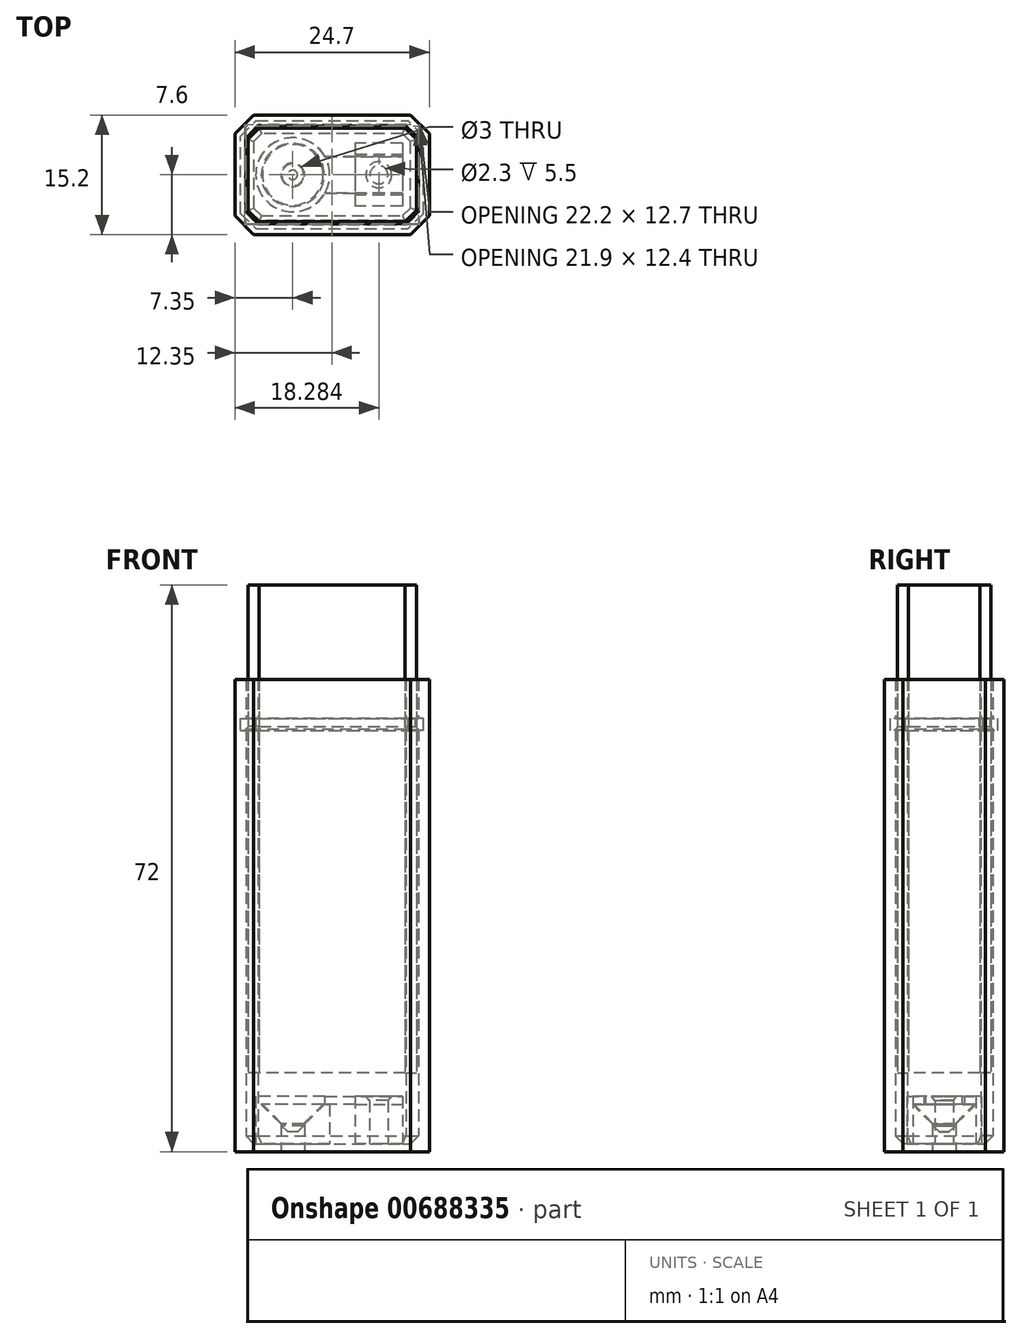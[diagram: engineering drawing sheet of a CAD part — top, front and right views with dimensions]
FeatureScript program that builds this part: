
annotation { "Feature Type Name" : "Feature", "Feature Type Description" : "" }
export const myFeature = defineFeature(function(context is Context, id is Id, definition is map)
    precondition{}
    {
        {
            var Q0;
            Q0=qCreatedBy(makeId("Top.planeOp"),FACE);
            cPlane(context, id + "F0", {"entities" : qUnion([Q0]), "cplaneType" : CPlaneType.OFFSET, "offset" : 10 * mm, "width" : 150 * mm, "height" : 150 * mm});
        }
        {
            var Q0;
            Q0=qCreatedBy(id+"F0.planeOp",FACE);
            var sketch = newSketch(context, id + "F1", { "sketchPlane" : qUnion([Q0])});
            skLineSegment(sketch, "E0.bottom", {"start": v(9.29, 5.95) * mm, "end": v(-9.29, 5.95) * mm});
            skLineSegment(sketch, "E0.top", {"start": v(9.29, -5.95) * mm, "end": v(-9.29, -5.95) * mm});
            skLineSegment(sketch, "E0.left", {"start": v(10.7, 4.54) * mm, "end": v(10.7, -4.54) * mm});
            skLineSegment(sketch, "E0.right", {"start": v(-10.7, 4.54) * mm, "end": v(-10.7, -4.54) * mm});
            skPoint(sketch, "E0.middle", {"position": v(0, 0) * mm});
            skLineSegment(sketch, "E1", {"start": v(9.29, 5.95) * mm, "end": v(10.7, 4.54) * mm});
            skPoint(sketch, "E2.orphan", {"position": v(10.7, 5.95) * mm});
            skLineSegment(sketch, "E3.MirrorCS", {"start": v(9.29, -5.95) * mm, "end": v(10.7, -4.54) * mm});
            skLineSegment(sketch, "E4.MirrorCS", {"start": v(-9.29, 5.95) * mm, "end": v(-10.7, 4.54) * mm});
            skLineSegment(sketch, "E5.MirrorCS", {"start": v(-9.29, -5.95) * mm, "end": v(-10.7, -4.54) * mm});
            skPoint(sketch, "E6.orphan", {"position": v(10.7, -5.95) * mm});
            skPoint(sketch, "E7.orphan", {"position": v(-10.7, -5.95) * mm});
            skPoint(sketch, "E8.orphan", {"position": v(-10.7, 5.95) * mm});
            skSolve(sketch);
        }
        {
            var Q0;
            Q0=makeQuery(id+"F1.imprint","IMPRINT",FACE,{"disambiguationData":[TD([[makeQuery(id+"F1.imprint","IMPRINT",EDGE,{"derivedFrom":sQuery(id+"F1.wireOp",EDGE,"E0.bottom")}),1.0]])]});
            extrude(context, id + "F2", {"entities" : qUnion([Q0]), "depth" : 62 * mm, "offsetDistance" : 25 * mm});
        }
        {
            var Q0;
            Q0=qCreatedBy(makeId("Top.planeOp"),FACE);
            var sketch = newSketch(context, id + "F3", { "sketchPlane" : qUnion([Q0])});
            skLineSegment(sketch, "E9.0", {"start": v(12.35, -5.22) * mm, "end": v(9.97, -7.6) * mm});
            skLineSegment(sketch, "E9.1", {"start": v(12.35, 5.22) * mm, "end": v(12.35, -5.22) * mm});
            skLineSegment(sketch, "E9.2", {"start": v(9.97, -7.6) * mm, "end": v(-9.97, -7.6) * mm});
            skLineSegment(sketch, "E9.3", {"start": v(9.97, 7.6) * mm, "end": v(12.35, 5.22) * mm});
            skLineSegment(sketch, "E9.4", {"start": v(-9.97, -7.6) * mm, "end": v(-12.35, -5.22) * mm});
            skLineSegment(sketch, "E9.5", {"start": v(-12.35, -5.22) * mm, "end": v(-12.35, 5.22) * mm});
            skLineSegment(sketch, "E9.6", {"start": v(-12.35, 5.22) * mm, "end": v(-9.97, 7.6) * mm});
            skLineSegment(sketch, "E9.7", {"start": v(-9.97, 7.6) * mm, "end": v(9.97, 7.6) * mm});
            skSolve(sketch);
        }
        {
            var Q0;
            Q0=makeQuery(id+"F3.imprint","IMPRINT",FACE,{"disambiguationData":[TD([[makeQuery(id+"F3.imprint","IMPRINT",EDGE,{"derivedFrom":sQuery(id+"F3.wireOp",EDGE,"E9.0")}),-1.0]])]});
            extrude(context, id + "F4", {"entities" : qUnion([Q0]), "depth" : 60 * mm, "offsetDistance" : 25 * mm});
        }
        {
            var Q0;
            Q0=makeQuery(id+"F2.opExtrude","SWEPT_BODY",BODY,{"disambiguationData":[OSD([sQuery(id+"F1.wireOp",EDGE,"E0.bottom"),sQuery(id+"F1.wireOp",EDGE,"E0.top"),sQuery(id+"F1.wireOp",EDGE,"E0.left"),sQuery(id+"F1.wireOp",EDGE,"E0.right"),sQuery(id+"F1.wireOp",EDGE,"E1"),sQuery(id+"F1.wireOp",EDGE,"E3.MirrorCS"),sQuery(id+"F1.wireOp",EDGE,"E4.MirrorCS"),sQuery(id+"F1.wireOp",EDGE,"E5.MirrorCS")])]});
            var Q1;
            Q1=makeQuery(id+"F4.opExtrude","SWEPT_BODY",BODY,{"disambiguationData":[OSD([sQuery(id+"F3.wireOp",EDGE,"E9.0"),sQuery(id+"F3.wireOp",EDGE,"E9.1"),sQuery(id+"F3.wireOp",EDGE,"E9.2"),sQuery(id+"F3.wireOp",EDGE,"E9.3"),sQuery(id+"F3.wireOp",EDGE,"E9.4"),sQuery(id+"F3.wireOp",EDGE,"E9.5"),sQuery(id+"F3.wireOp",EDGE,"E9.6"),sQuery(id+"F3.wireOp",EDGE,"E9.7")])]});
            var Q2;
            Q2=makeQuery(id+"F2.opExtrude","SWEPT_FACE",FACE,{"disambiguationData":[OSD([sQuery(id+"F1.wireOp",EDGE,"E0.top")])]});
            var Q3;
            Q3=makeQuery(id+"F2.opExtrude","SWEPT_FACE",FACE,{"disambiguationData":[OSD([sQuery(id+"F1.wireOp",EDGE,"E3.MirrorCS")])]});
            var Q4;
            Q4=makeQuery(id+"F2.opExtrude","SWEPT_FACE",FACE,{"disambiguationData":[OSD([sQuery(id+"F1.wireOp",EDGE,"E0.left")])]});
            var Q5;
            Q5=makeQuery(id+"F2.opExtrude","SWEPT_FACE",FACE,{"disambiguationData":[OSD([sQuery(id+"F1.wireOp",EDGE,"E0.bottom")])]});
            var Q6;
            Q6=makeQuery(id+"F2.opExtrude","SWEPT_FACE",FACE,{"disambiguationData":[OSD([sQuery(id+"F1.wireOp",EDGE,"E4.MirrorCS")])]});
            var Q7;
            Q7=makeQuery(id+"F2.opExtrude","SWEPT_FACE",FACE,{"disambiguationData":[OSD([sQuery(id+"F1.wireOp",EDGE,"E0.right")])]});
            var Q8;
            Q8=makeQuery(id+"F2.opExtrude","SWEPT_FACE",FACE,{"disambiguationData":[OSD([sQuery(id+"F1.wireOp",EDGE,"E5.MirrorCS")])]});
            var Q9;
            Q9=makeQuery(id+"F2.opExtrude","SWEPT_FACE",FACE,{"disambiguationData":[OSD([sQuery(id+"F1.wireOp",EDGE,"E1")])]});
            booleanBodies(context, id + "F5", {"operationType" : BooleanOperationType.SUBTRACTION, "tools" : qUnion([Q0]), "targets" : qUnion([Q1]), "offset" : true, "entitiesToOffset" : qUnion([Q2, Q3, Q4, Q5, Q6, Q7, Q8, Q9]), "offsetDistance" : .25 * mm, "keepTools" : true});
        }
        {
            var Q0;
            Q0=makeQuery(id+"F5.tempBoolean.opBoolean","COPY",FACE,{"derivedFrom":makeQuery(id+"F5.offsetTempBody.opPattern","COPY",FACE,{"derivedFrom":makeQuery(id+"F2.opExtrude","CAP_FACE",FACE,{"disambiguationData":[OSD([sQuery(id+"F1.wireOp",EDGE,"E0.bottom"),sQuery(id+"F1.wireOp",EDGE,"E0.top"),sQuery(id+"F1.wireOp",EDGE,"E0.left"),sQuery(id+"F1.wireOp",EDGE,"E0.right"),sQuery(id+"F1.wireOp",EDGE,"E1"),sQuery(id+"F1.wireOp",EDGE,"E3.MirrorCS"),sQuery(id+"F1.wireOp",EDGE,"E4.MirrorCS"),sQuery(id+"F1.wireOp",EDGE,"E5.MirrorCS")])],"isStart":true}),"instanceName":"1"})});
            var Q1;
            Q1=makeQuery(id+"F4.opExtrude","CAP_FACE",FACE,{"disambiguationData":[OSD([sQuery(id+"F3.wireOp",EDGE,"E9.0"),sQuery(id+"F3.wireOp",EDGE,"E9.1"),sQuery(id+"F3.wireOp",EDGE,"E9.2"),sQuery(id+"F3.wireOp",EDGE,"E9.3"),sQuery(id+"F3.wireOp",EDGE,"E9.4"),sQuery(id+"F3.wireOp",EDGE,"E9.5"),sQuery(id+"F3.wireOp",EDGE,"E9.6"),sQuery(id+"F3.wireOp",EDGE,"E9.7")])],"isStart":true});
            extrude(context, id + "F6", {"entities" : qUnion([Q0]), "operationType" : NewBodyOperationType.REMOVE, "endBound" : BoundingType.UP_TO_SURFACE, "oppositeDirection" : true, "depth" : 25 * mm, "endBoundEntityFace" : qUnion([Q1]), "hasOffset" : true, "offsetDistance" : 1 * mm});
        }
        {
            var Q0;
            Q0=makeQuery(id+"F6.boolean.opBoolean","COPY",EDGE,{"derivedFrom":makeQuery(id+"F6.opExtrude","CAP_EDGE",EDGE,{"disambiguationData":[OSD([sQuery(id+"F1.wireOp",EDGE,"E0.left")])],"isStart":false})});
            var Q1;
            Q1=makeQuery(id+"F6.boolean.opBoolean","COPY",EDGE,{"derivedFrom":makeQuery(id+"F6.opExtrude","CAP_EDGE",EDGE,{"disambiguationData":[OSD([sQuery(id+"F1.wireOp",EDGE,"E3.MirrorCS")])],"isStart":false})});
            var Q2;
            Q2=makeQuery(id+"F6.boolean.opBoolean","COPY",EDGE,{"derivedFrom":makeQuery(id+"F6.opExtrude","CAP_EDGE",EDGE,{"disambiguationData":[OSD([sQuery(id+"F1.wireOp",EDGE,"E0.top")])],"isStart":false})});
            var Q3;
            Q3=makeQuery(id+"F6.boolean.opBoolean","COPY",EDGE,{"derivedFrom":makeQuery(id+"F6.opExtrude","CAP_EDGE",EDGE,{"disambiguationData":[OSD([sQuery(id+"F1.wireOp",EDGE,"E5.MirrorCS")])],"isStart":false})});
            var Q4;
            Q4=makeQuery(id+"F6.boolean.opBoolean","COPY",EDGE,{"derivedFrom":makeQuery(id+"F6.opExtrude","CAP_EDGE",EDGE,{"disambiguationData":[OSD([sQuery(id+"F1.wireOp",EDGE,"E0.right")])],"isStart":false})});
            var Q5;
            Q5=makeQuery(id+"F6.boolean.opBoolean","COPY",EDGE,{"derivedFrom":makeQuery(id+"F6.opExtrude","CAP_EDGE",EDGE,{"disambiguationData":[OSD([sQuery(id+"F1.wireOp",EDGE,"E4.MirrorCS")])],"isStart":false})});
            var Q6;
            Q6=makeQuery(id+"F6.boolean.opBoolean","COPY",EDGE,{"derivedFrom":makeQuery(id+"F6.opExtrude","CAP_EDGE",EDGE,{"disambiguationData":[OSD([sQuery(id+"F1.wireOp",EDGE,"E0.bottom")])],"isStart":false})});
            var Q7;
            Q7=makeQuery(id+"F6.boolean.opBoolean","COPY",EDGE,{"derivedFrom":makeQuery(id+"F6.opExtrude","CAP_EDGE",EDGE,{"disambiguationData":[OSD([sQuery(id+"F1.wireOp",EDGE,"E1")])],"isStart":false})});
            chamfer(context, id + "F7", {"entities" : qUnion([Q0, Q1, Q2, Q3, Q4, Q5, Q6, Q7]), "width" : 1 * mm, "tangentPropagation" : true});
        }
        {
            var Q0;
            Q0=makeQuery(id+"F6.boolean.opBoolean","COPY",FACE,{"derivedFrom":makeQuery(id+"F6.opExtrude","CAP_FACE",FACE,{"disambiguationData":[OSD([sQuery(id+"F1.wireOp",EDGE,"E0.bottom"),sQuery(id+"F1.wireOp",EDGE,"E0.top"),sQuery(id+"F1.wireOp",EDGE,"E0.left"),sQuery(id+"F1.wireOp",EDGE,"E0.right"),sQuery(id+"F1.wireOp",EDGE,"E1"),sQuery(id+"F1.wireOp",EDGE,"E3.MirrorCS"),sQuery(id+"F1.wireOp",EDGE,"E4.MirrorCS"),sQuery(id+"F1.wireOp",EDGE,"E5.MirrorCS")])],"isStart":false})});
            var sketch = newSketch(context, id + "F8", { "sketchPlane" : qUnion([Q0])});
            skCircle(sketch, "E10", {"center": v(-5, 0) * mm, "radius": 1.5 * mm});
            skCircle(sketch, "E11", {"center": v(-5, 0) * mm, "radius": 4.7 * mm});
            skSolve(sketch);
        }
        {
            var Q0;
            Q0=makeQuery(id+"F8.imprint","IMPRINT",FACE,{"disambiguationData":[TD([[makeQuery(id+"F8.imprint","IMPRINT",EDGE,{"derivedFrom":sQuery(id+"F8.wireOp",EDGE,"E10")}),-1.0]])]});
            extrude(context, id + "F9", {"entities" : qUnion([Q0]), "operationType" : NewBodyOperationType.ADD, "depth" : 5 * mm, "offsetDistance" : 25 * mm});
        }
        {
            var Q0;
            Q0=makeQuery(id+"F9.boolean.opBoolean","SPLIT",FACE,{"disambiguationData":[TD([makeQuery(id+"F9.opExtrude","SWEPT_FACE",FACE,{"disambiguationData":[OSD([sQuery(id+"F8.wireOp",EDGE,"E10")])]})])],"derivedFrom":makeQuery(id+"F6.boolean.opBoolean","COPY",FACE,{"derivedFrom":makeQuery(id+"F6.opExtrude","CAP_FACE",FACE,{"disambiguationData":[OSD([sQuery(id+"F1.wireOp",EDGE,"E0.bottom"),sQuery(id+"F1.wireOp",EDGE,"E0.top"),sQuery(id+"F1.wireOp",EDGE,"E0.left"),sQuery(id+"F1.wireOp",EDGE,"E0.right"),sQuery(id+"F1.wireOp",EDGE,"E1"),sQuery(id+"F1.wireOp",EDGE,"E3.MirrorCS"),sQuery(id+"F1.wireOp",EDGE,"E4.MirrorCS"),sQuery(id+"F1.wireOp",EDGE,"E5.MirrorCS")])],"isStart":false})})});
            extrude(context, id + "F10", {"entities" : qUnion([Q0]), "operationType" : NewBodyOperationType.REMOVE, "endBound" : BoundingType.THROUGH_ALL, "oppositeDirection" : true, "depth" : 25 * mm, "offsetDistance" : 25 * mm});
        }
        {
            var Q0;
            Q0=makeQuery(id+"F9.opExtrude","CAP_EDGE",EDGE,{"disambiguationData":[OSD([sQuery(id+"F8.wireOp",EDGE,"E10")])],"isStart":false});
            chamfer(context, id + "F11", {"entities" : qUnion([Q0]), "width" : 2.5 * mm, "tangentPropagation" : true});
        }
        {
            var Q0;
            Q0=makeQuery(id+"F9.opExtrude","CAP_FACE",FACE,{"disambiguationData":[OSD([sQuery(id+"F8.wireOp",EDGE,"E10"),sQuery(id+"F8.wireOp",EDGE,"E11")])],"isStart":false});
            var sketch = newSketch(context, id + "F12", { "sketchPlane" : qUnion([Q0])});
            skCircle(sketch, "E12.0", {"center": v(-5, 0) * mm, "radius": 4.7 * mm});
            skSolve(sketch);
        }
        {
            var Q0;
            Q0 = qSketchRegion(id + "F12", true);
            var Q1;
            Q1=makeQuery(id+"F4.opExtrude","CAP_FACE",FACE,{"disambiguationData":[OSD([sQuery(id+"F3.wireOp",EDGE,"E9.0"),sQuery(id+"F3.wireOp",EDGE,"E9.1"),sQuery(id+"F3.wireOp",EDGE,"E9.2"),sQuery(id+"F3.wireOp",EDGE,"E9.3"),sQuery(id+"F3.wireOp",EDGE,"E9.4"),sQuery(id+"F3.wireOp",EDGE,"E9.5"),sQuery(id+"F3.wireOp",EDGE,"E9.6"),sQuery(id+"F3.wireOp",EDGE,"E9.7")])],"isStart":true});
            extrude(context, id + "F13", {"entities" : qUnion([Q0]), "depth" : 1 * mm, "offsetDistance" : 25 * mm, "hasSecondDirection" : true, "secondDirectionBound" : SecondDirectionBoundingType.UP_TO_SURFACE, "secondDirectionOppositeDirection" : true, "secondDirectionDepth" : 25 * mm, "secondDirectionBoundEntityFace" : qUnion([Q1]), "hasSecondDirectionOffset" : true, "secondDirectionOffsetDistance" : 2.5 * mm});
        }
        {
            var Q0;
            Q0=makeQuery(id+"F4.opExtrude","SWEPT_BODY",BODY,{"disambiguationData":[OSD([sQuery(id+"F3.wireOp",EDGE,"E9.0"),sQuery(id+"F3.wireOp",EDGE,"E9.1"),sQuery(id+"F3.wireOp",EDGE,"E9.2"),sQuery(id+"F3.wireOp",EDGE,"E9.3"),sQuery(id+"F3.wireOp",EDGE,"E9.4"),sQuery(id+"F3.wireOp",EDGE,"E9.5"),sQuery(id+"F3.wireOp",EDGE,"E9.6"),sQuery(id+"F3.wireOp",EDGE,"E9.7")])]});
            var Q1;
            Q1=makeQuery(id+"F13.opExtrude","SWEPT_BODY",BODY,{"disambiguationData":[OSD([sQuery(id+"F12.wireOp",EDGE,"E12.0")])]});
            var Q2;
            Q2=makeQuery(id+"F11.opChamfer","BLEND_FACE",FACE,{"disambiguationData":[OSD([sQuery(id+"F8.wireOp",EDGE,"E10")])]});
            var Q3;
            {var subQ0=sQuery(id+"F8.wireOp",EDGE,"E10");Q3=makeQuery(id+"F10.boolean.opBoolean","MERGE",FACE,{"derivedFrom":[makeQuery(id+"F9.opExtrude","SWEPT_FACE",FACE,{"disambiguationData":[OSD([subQ0])]}),makeQuery(id+"F10.opExtrude","SWEPT_FACE",FACE,{"disambiguationData":[OSD([subQ0])]})]});}
            booleanBodies(context, id + "F14", {"operationType" : BooleanOperationType.SUBTRACTION, "tools" : qUnion([Q0]), "targets" : qUnion([Q1]), "offset" : true, "entitiesToOffset" : qUnion([Q2, Q3]), "offsetDistance" : .1 * mm, "keepTools" : true});
        }
        {
            var Q0;
            {var subQ0=sQuery(id+"F8.wireOp",EDGE,"E10");Q0=makeQuery(id+"F14.tempBoolean.opBoolean","INTERSECT",EDGE,{"derivedFrom":[makeQuery(id+"F13.opExtrude","CAP_FACE",FACE,{"disambiguationData":[OSD([sQuery(id+"F12.wireOp",EDGE,"E12.0")])],"isStart":true}),makeQuery(id+"F14.offsetTempBody.opPattern","COPY",FACE,{"derivedFrom":makeQuery(id+"F10.boolean.opBoolean","MERGE",FACE,{"derivedFrom":[makeQuery(id+"F9.opExtrude","SWEPT_FACE",FACE,{"disambiguationData":[OSD([subQ0])]})],"fromTools":[makeQuery(id+"F10.opExtrude","SWEPT_FACE",FACE,{"disambiguationData":[OSD([subQ0])]})]}),"instanceName":"1"})]});}
            chamfer(context, id + "F15", {"entities" : qUnion([Q0]), "width" : 0.8 * mm, "tangentPropagation" : true});
        }
        {
            var Q0;
            {var subQ0=sQuery(id+"F1.wireOp",EDGE,"E0.right");var subQ1=sQuery(id+"F1.wireOp",EDGE,"E0.left");var subQ2=sQuery(id+"F1.wireOp",EDGE,"E0.top");var subQ3=sQuery(id+"F1.wireOp",EDGE,"E0.bottom");var subQ4=sQuery(id+"F1.wireOp",EDGE,"E1");var subQ5=sQuery(id+"F1.wireOp",EDGE,"E3.MirrorCS");var subQ6=sQuery(id+"F1.wireOp",EDGE,"E4.MirrorCS");var subQ7=sQuery(id+"F1.wireOp",EDGE,"E5.MirrorCS");Q0=makeQuery(id+"F9.boolean.opBoolean","SPLIT",FACE,{"disambiguationData":[TD([makeQuery(id+"F7.opChamfer","BLEND_FACE",FACE,{"disambiguationData":[OSD([subQ3])]})])],"derivedFrom":makeQuery(id+"F6.boolean.opBoolean","COPY",FACE,{"derivedFrom":makeQuery(id+"F6.opExtrude","CAP_FACE",FACE,{"disambiguationData":[OSD([subQ3,subQ2,subQ1,subQ0,subQ4,subQ5,subQ6,subQ7])],"isStart":false})})});}
            var sketch = newSketch(context, id + "F16", { "sketchPlane" : qUnion([Q0])});
            skLineSegment(sketch, "E13.bottom", {"start": v(8.93, 4) * mm, "end": v(2.93, 4) * mm});
            skLineSegment(sketch, "E13.top", {"start": v(8.93, -4) * mm, "end": v(2.93, -4) * mm});
            skLineSegment(sketch, "E13.left", {"start": v(8.93, 4) * mm, "end": v(8.93, -4) * mm});
            skLineSegment(sketch, "E13.right", {"start": v(2.93, 4) * mm, "end": v(2.93, -4) * mm});
            skPoint(sketch, "E13.middle", {"position": v(5.93, 0) * mm});
            skCircle(sketch, "E14", {"center": v(5.93, 0) * mm, "radius": 1.15 * mm});
            skSolve(sketch);
        }
        {
            var Q0;
            Q0=makeQuery(id+"F16.imprint","IMPRINT",FACE,{"disambiguationData":[TD([[makeQuery(id+"F16.imprint","IMPRINT",EDGE,{"derivedFrom":sQuery(id+"F16.wireOp",EDGE,"E13.bottom")}),1.0]])]});
            var Q1;
            Q1=makeQuery(id+"F9.opExtrude","CAP_FACE",FACE,{"disambiguationData":[OSD([sQuery(id+"F8.wireOp",EDGE,"E10"),sQuery(id+"F8.wireOp",EDGE,"E11")])],"isStart":false});
            extrude(context, id + "F17", {"entities" : qUnion([Q0]), "operationType" : NewBodyOperationType.ADD, "endBound" : BoundingType.UP_TO_SURFACE, "depth" : 25 * mm, "endBoundEntityFace" : qUnion([Q1]), "offsetDistance" : 25 * mm});
        }
        {
            var Q0;
            Q0=makeQuery(id+"F17.opExtrude","CAP_FACE",FACE,{"disambiguationData":[OSD([sQuery(id+"F16.wireOp",EDGE,"E13.bottom"),sQuery(id+"F16.wireOp",EDGE,"E13.top"),sQuery(id+"F16.wireOp",EDGE,"E13.left"),sQuery(id+"F16.wireOp",EDGE,"E13.right"),sQuery(id+"F16.wireOp",EDGE,"E14")])],"isStart":false});
            var sketch = newSketch(context, id + "F18", { "sketchPlane" : qUnion([Q0])});
            skLineSegment(sketch, "E15.bottom", {"start": v(2.93, 4) * mm, "end": v(8.93, 4) * mm});
            skLineSegment(sketch, "E15.top", {"start": v(2.93, 2.6) * mm, "end": v(8.93, 2.6) * mm});
            skLineSegment(sketch, "E15.left", {"start": v(2.93, 4) * mm, "end": v(2.93, 2.6) * mm});
            skLineSegment(sketch, "E15.right", {"start": v(8.93, 4) * mm, "end": v(8.93, 2.6) * mm});
            skLineSegment(sketch, "E16.bottom", {"start": v(8.93, -4) * mm, "end": v(2.93, -4) * mm});
            skLineSegment(sketch, "E16.top", {"start": v(8.93, -2.6) * mm, "end": v(2.93, -2.6) * mm});
            skLineSegment(sketch, "E16.left", {"start": v(8.93, -4) * mm, "end": v(8.93, -2.6) * mm});
            skLineSegment(sketch, "E16.right", {"start": v(2.93, -4) * mm, "end": v(2.93, -2.6) * mm});
            skSolve(sketch);
        }
        {
            var Q0;
            Q0 = qSketchRegion(id + "F18", true);
            extrude(context, id + "F19", {"entities" : qUnion([Q0]), "operationType" : NewBodyOperationType.ADD, "depth" : 1 * mm, "offsetDistance" : 25 * mm});
        }
        {
            var Q0;
            Q0=makeQuery(id+"F13.opExtrude","CAP_FACE",FACE,{"disambiguationData":[OSD([sQuery(id+"F12.wireOp",EDGE,"E12.0")])],"isStart":false});
            var sketch = newSketch(context, id + "F20", { "sketchPlane" : qUnion([Q0])});
            skArc(sketch, "E17.0", {"start": v(-0.9, -2.3) * mm, "mid": v(-0.3, 0) * mm, "end": v(-0.9, 2.3) * mm});
            skCircle(sketch, "E18.0", {"center": v(5.93, 0) * mm, "radius": 1.15 * mm});
            skLineSegment(sketch, "E19.0", {"start": v(2.93, 2.3) * mm, "end": v(8.93, 2.3) * mm});
            skLineSegment(sketch, "E20.MirrorCS", {"start": v(2.93, -2.3) * mm, "end": v(8.93, -2.3) * mm});
            skLineSegment(sketch, "E21", {"start": v(8.93, 2.3) * mm, "end": v(8.93, -2.3) * mm});
            skLineSegment(sketch, "E22", {"start": v(2.93, 2.3) * mm, "end": v(-0.9, 2.3) * mm});
            skLineSegment(sketch, "E23", {"start": v(2.93, -2.3) * mm, "end": v(-0.9, -2.3) * mm});
            skSolve(sketch);
        }
        {
            var Q0;
            Q0=makeQuery(id+"F20.imprint","IMPRINT",FACE,{"disambiguationData":[TD([[makeQuery(id+"F20.imprint","IMPRINT",EDGE,{"derivedFrom":sQuery(id+"F20.wireOp",EDGE,"E17.0")}),-1.0]])]});
            var Q1;
            Q1=makeQuery(id+"F17.opExtrude","CAP_FACE",FACE,{"disambiguationData":[OSD([sQuery(id+"F16.wireOp",EDGE,"E13.bottom"),sQuery(id+"F16.wireOp",EDGE,"E13.top"),sQuery(id+"F16.wireOp",EDGE,"E13.left"),sQuery(id+"F16.wireOp",EDGE,"E13.right"),sQuery(id+"F16.wireOp",EDGE,"E14")])],"isStart":false});
            extrude(context, id + "F21", {"entities" : qUnion([Q0]), "operationType" : NewBodyOperationType.ADD, "endBound" : BoundingType.UP_TO_SURFACE, "oppositeDirection" : true, "depth" : 25 * mm, "endBoundEntityFace" : qUnion([Q1]), "offsetDistance" : 25 * mm});
        }
        {
            var Q0;
            Q0=makeQuery(id+"F21.opExtrude","CAP_EDGE",EDGE,{"disambiguationData":[OSD([sQuery(id+"F20.wireOp",EDGE,"E18.0")])],"isStart":true});
            chamfer(context, id + "F22", {"entities" : qUnion([Q0]), "width" : .5 * mm, "tangentPropagation" : true});
        }
        {
            var Q0;
            Q0=makeQuery(id+"F4.opExtrude","CAP_FACE",FACE,{"disambiguationData":[OSD([sQuery(id+"F3.wireOp",EDGE,"E9.0"),sQuery(id+"F3.wireOp",EDGE,"E9.1"),sQuery(id+"F3.wireOp",EDGE,"E9.2"),sQuery(id+"F3.wireOp",EDGE,"E9.3"),sQuery(id+"F3.wireOp",EDGE,"E9.4"),sQuery(id+"F3.wireOp",EDGE,"E9.5"),sQuery(id+"F3.wireOp",EDGE,"E9.6"),sQuery(id+"F3.wireOp",EDGE,"E9.7")])],"isStart":false});
            cPlane(context, id + "F23", {"entities" : qUnion([Q0]), "cplaneType" : CPlaneType.OFFSET, "offset" : 5 * mm, "oppositeDirection" : true, "width" : 150 * mm, "height" : 150 * mm});
        }
        {
            var Q0;
            Q0=qCreatedBy(id+"F23.planeOp",FACE);
            var sketch = newSketch(context, id + "F24", { "sketchPlane" : qUnion([Q0])});
            skLineSegment(sketch, "E24.0", {"start": v(-10.6, -4.5) * mm, "end": v(-9.24, -5.85) * mm});
            skLineSegment(sketch, "E24.1", {"start": v(-9.24, -5.85) * mm, "end": v(9.24, -5.85) * mm});
            skLineSegment(sketch, "E24.2", {"start": v(-10.6, -4.5) * mm, "end": v(-10.6, 4.5) * mm});
            skLineSegment(sketch, "E24.3", {"start": v(10.6, -4.5) * mm, "end": v(9.24, -5.85) * mm});
            skLineSegment(sketch, "E24.4", {"start": v(-10.6, 4.5) * mm, "end": v(-9.24, 5.85) * mm});
            skLineSegment(sketch, "E24.5", {"start": v(-9.24, 5.85) * mm, "end": v(9.24, 5.85) * mm});
            skLineSegment(sketch, "E24.6", {"start": v(10.6, 4.5) * mm, "end": v(9.24, 5.85) * mm});
            skLineSegment(sketch, "E24.7", {"start": v(10.6, -4.5) * mm, "end": v(10.6, 4.5) * mm});
            skLineSegment(sketch, "E25.0", {"start": v(-11.6, -4.9) * mm, "end": v(-11.6, 4.9) * mm});
            skLineSegment(sketch, "E25.1", {"start": v(-11.6, -4.9) * mm, "end": v(-9.66, -6.85) * mm});
            skLineSegment(sketch, "E25.2", {"start": v(-11.6, 4.9) * mm, "end": v(-9.66, 6.85) * mm});
            skLineSegment(sketch, "E25.3", {"start": v(-9.66, -6.85) * mm, "end": v(9.66, -6.85) * mm});
            skLineSegment(sketch, "E25.4", {"start": v(-9.66, 6.85) * mm, "end": v(9.66, 6.85) * mm});
            skLineSegment(sketch, "E25.5", {"start": v(11.6, 4.9) * mm, "end": v(9.66, 6.85) * mm});
            skLineSegment(sketch, "E25.6", {"start": v(11.6, -4.9) * mm, "end": v(11.6, 4.9) * mm});
            skLineSegment(sketch, "E25.7", {"start": v(11.6, -4.9) * mm, "end": v(9.66, -6.85) * mm});
            skSolve(sketch);
        }
        {
            var Q0;
            Q0 = qSketchRegion(id + "F24", true);
            extrude(context, id + "F25", {"entities" : qUnion([Q0]), "oppositeDirection" : true, "depth" : 1.5 * mm, "offsetDistance" : 25 * mm});
        }
        {
            var Q0;
            Q0=makeQuery(id+"F25.opExtrude","CAP_EDGE",EDGE,{"disambiguationData":[OSD([sQuery(id+"F24.wireOp",EDGE,"E24.1")])],"isStart":false});
            var Q1;
            Q1=makeQuery(id+"F25.opExtrude","CAP_EDGE",EDGE,{"disambiguationData":[OSD([sQuery(id+"F24.wireOp",EDGE,"E24.0")])],"isStart":false});
            var Q2;
            Q2=makeQuery(id+"F25.opExtrude","CAP_EDGE",EDGE,{"disambiguationData":[OSD([sQuery(id+"F24.wireOp",EDGE,"E24.2")])],"isStart":false});
            var Q3;
            Q3=makeQuery(id+"F25.opExtrude","CAP_EDGE",EDGE,{"disambiguationData":[OSD([sQuery(id+"F24.wireOp",EDGE,"E24.4")])],"isStart":false});
            var Q4;
            Q4=makeQuery(id+"F25.opExtrude","CAP_EDGE",EDGE,{"disambiguationData":[OSD([sQuery(id+"F24.wireOp",EDGE,"E24.5")])],"isStart":false});
            var Q5;
            Q5=makeQuery(id+"F25.opExtrude","CAP_EDGE",EDGE,{"disambiguationData":[OSD([sQuery(id+"F24.wireOp",EDGE,"E24.6")])],"isStart":false});
            var Q6;
            Q6=makeQuery(id+"F25.opExtrude","CAP_EDGE",EDGE,{"disambiguationData":[OSD([sQuery(id+"F24.wireOp",EDGE,"E24.7")])],"isStart":false});
            var Q7;
            Q7=makeQuery(id+"F25.opExtrude","CAP_EDGE",EDGE,{"disambiguationData":[OSD([sQuery(id+"F24.wireOp",EDGE,"E24.3")])],"isStart":false});
            chamfer(context, id + "F26", {"entities" : qUnion([Q0, Q1, Q2, Q3, Q4, Q5, Q6, Q7]), "width" : .5 * mm, "tangentPropagation" : true});
        }
        {
            var Q0;
            Q0=makeQuery(id+"F25.opExtrude","SWEPT_BODY",BODY,{"disambiguationData":[OSD([sQuery(id+"F24.wireOp",EDGE,"E24.0"),sQuery(id+"F24.wireOp",EDGE,"E24.1"),sQuery(id+"F24.wireOp",EDGE,"E24.2"),sQuery(id+"F24.wireOp",EDGE,"E24.3"),sQuery(id+"F24.wireOp",EDGE,"E24.4"),sQuery(id+"F24.wireOp",EDGE,"E24.5"),sQuery(id+"F24.wireOp",EDGE,"E24.6"),sQuery(id+"F24.wireOp",EDGE,"E24.7"),sQuery(id+"F24.wireOp",EDGE,"E25.0"),sQuery(id+"F24.wireOp",EDGE,"E25.1"),sQuery(id+"F24.wireOp",EDGE,"E25.2"),sQuery(id+"F24.wireOp",EDGE,"E25.3"),sQuery(id+"F24.wireOp",EDGE,"E25.4"),sQuery(id+"F24.wireOp",EDGE,"E25.5"),sQuery(id+"F24.wireOp",EDGE,"E25.6"),sQuery(id+"F24.wireOp",EDGE,"E25.7")])]});
            var Q1;
            Q1=makeQuery(id+"F4.opExtrude","SWEPT_BODY",BODY,{"disambiguationData":[OSD([sQuery(id+"F3.wireOp",EDGE,"E9.0"),sQuery(id+"F3.wireOp",EDGE,"E9.1"),sQuery(id+"F3.wireOp",EDGE,"E9.2"),sQuery(id+"F3.wireOp",EDGE,"E9.3"),sQuery(id+"F3.wireOp",EDGE,"E9.4"),sQuery(id+"F3.wireOp",EDGE,"E9.5"),sQuery(id+"F3.wireOp",EDGE,"E9.6"),sQuery(id+"F3.wireOp",EDGE,"E9.7")])]});
            booleanBodies(context, id + "F27", {"operationType" : BooleanOperationType.SUBTRACTION, "tools" : qUnion([Q0]), "targets" : qUnion([Q1]), "keepTools" : true});
        }
    });
